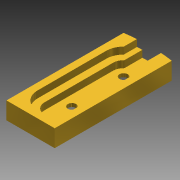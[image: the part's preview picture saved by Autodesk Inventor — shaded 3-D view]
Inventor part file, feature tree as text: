
AUTODESK INVENTOR PART (.ipt)
format: ipt  version: 2014 (Build 180170000, 170)  size: 192,000 bytes
history: native  units: in
note: dims shown in document units (in); Inventor stores cm internally (conversion verified against a paired STEP export)
features: extrude x9, sketch x9, plane x1, pattern_circular x1
ambient origin geometry x8: Origin, YZ Plane, XZ Plane, XY Plane, X Axis, Y Axis, Z Axis, Center Point
bodies: Solid1 (feature_tree)
feature tree (20):
  extrude  "Extrusion1"  Depth=0.25in TaperAngle=0.0deg
  extrude  "Extrusion2"  Depth=0.3in
  extrude  "Extrusion3"  Depth=0.2in TaperAngle=0.0deg
  extrude  "Extrusion4"  Depth=0.1in TaperAngle=0.0deg
  extrude  "Extrusion5"  Depth=0.1in TaperAngle=0.0deg
  extrude  "Extrusion6"  Depth=0.1in TaperAngle=0.0deg
  extrude  "Extrusion8"  Depth=0.25in
  plane  "Work Plane1"
  extrude  "Extrusion11"  Depth=0.1in TaperAngle=0.0deg
  pattern_circular  "Circular Pattern2"  [2 undecoded]
  extrude  "Extrusion12"  Depth=0.5in
  sketch  "Sketch1"  dims[d0=4.75in d1=0.25in d2=0.0in]
  sketch  "Sketch2"  dims[d3=1.0in d4=0.3in]
  sketch  "Sketch3"  dims[d5=2.0in d6=0.2in d7=0.0in]
  sketch  "Sketch4"  dims[d8=0.1in d9=0.1in d10=0.0in]
  sketch  "Sketch5"  dims[d11=0.2in d12=0.1in d13=0.0in]
  sketch  "Sketch6"  dims[d14=0.35in d15=0.1in d16=0.0in]
  sketch  "Sketch8"  dims[d17=0.25in d18=0.75in]
  sketch  "Sketch11"  dims[d19=0.12in d20=0.1in d21=0.0in]
  sketch  "Sketch12"  dims[d25=0.5in d26=1.0in d27=0.5in d28=0.025in d29=0.0in d41=0.135in d42=1.0in d43=0.0in d44=1.1811in d45=360.0deg d47=0.1in d48=0.1in d49=0.1in d50=1.0in d51=0.0in]
note: 2 required parameter values undecoded (feature->parameter linkage not recoverable at this tier; creation-order binding heuristic only, values carry confidence <= 0.55)
